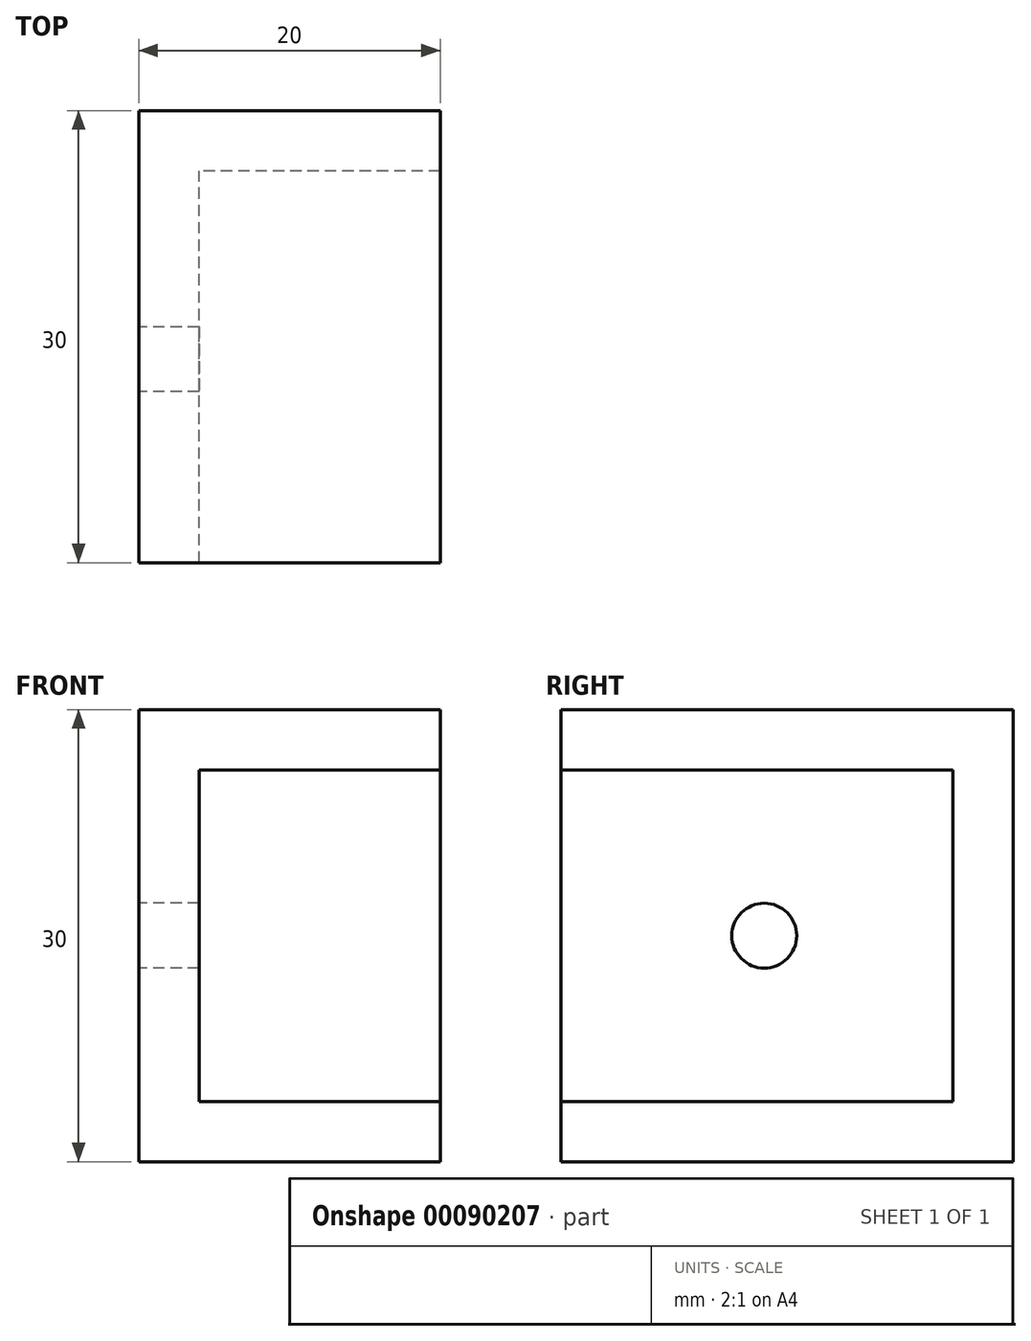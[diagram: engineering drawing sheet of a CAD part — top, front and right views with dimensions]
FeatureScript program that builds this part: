
annotation { "Feature Type Name" : "Feature", "Feature Type Description" : "" }
export const myFeature = defineFeature(function(context is Context, id is Id, definition is map)
    precondition{}
    {
        {
            var Q0;
            Q0=qCreatedBy(makeId("Top.planeOp"),FACE);
            var sketch = newSketch(context, id + "F0", { "sketchPlane" : qUnion([Q0])});
            skLineSegment(sketch, "E0", {"start": v(-8.2, -8.2) * mm, "end": v(-6.57, -8.2) * mm});
            skLineSegment(sketch, "E1", {"start": v(-8.2, -6.57) * mm, "end": v(-8.2, -8.2) * mm});
            skLineSegment(sketch, "E2", {"start": v(-7.66, -6.57) * mm, "end": v(-8.2, -6.57) * mm});
            skLineSegment(sketch, "E3", {"start": v(-6.57, -7.66) * mm, "end": v(-7.66, -6.57) * mm});
            skLineSegment(sketch, "E4", {"start": v(-6.57, -8.2) * mm, "end": v(-6.57, -7.66) * mm});
            skLineSegment(sketch, "E5", {"start": v(7.66, -6.57) * mm, "end": v(6.57, -7.66) * mm});
            skLineSegment(sketch, "E6", {"start": v(8.2, -6.57) * mm, "end": v(7.66, -6.57) * mm});
            skLineSegment(sketch, "E7", {"start": v(8.2, -8.2) * mm, "end": v(8.2, -6.57) * mm});
            skLineSegment(sketch, "E8", {"start": v(6.57, -8.2) * mm, "end": v(8.2, -8.2) * mm});
            skLineSegment(sketch, "E9", {"start": v(6.57, -7.66) * mm, "end": v(6.57, -8.2) * mm});
            skCircle(sketch, "E10", {"center": v(0, 0) * mm, "radius": 2.1 * mm});
            skLineSegment(sketch, "E11", {"start": v(8.2, 8.2) * mm, "end": v(6.57, 8.2) * mm});
            skLineSegment(sketch, "E12", {"start": v(8.2, 6.57) * mm, "end": v(8.2, 8.2) * mm});
            skLineSegment(sketch, "E13", {"start": v(7.66, 6.57) * mm, "end": v(8.2, 6.57) * mm});
            skLineSegment(sketch, "E14", {"start": v(6.57, 7.66) * mm, "end": v(7.66, 6.57) * mm});
            skLineSegment(sketch, "E15", {"start": v(6.57, 8.2) * mm, "end": v(6.57, 7.66) * mm});
            skLineSegment(sketch, "E16", {"start": v(-7.66, 6.57) * mm, "end": v(-6.57, 7.66) * mm});
            skLineSegment(sketch, "E17", {"start": v(-8.2, 6.57) * mm, "end": v(-7.66, 6.57) * mm});
            skLineSegment(sketch, "E18", {"start": v(-8.2, 8.2) * mm, "end": v(-8.2, 6.57) * mm});
            skLineSegment(sketch, "E19", {"start": v(-6.57, 8.2) * mm, "end": v(-8.2, 8.2) * mm});
            skLineSegment(sketch, "E20", {"start": v(-6.57, 7.66) * mm, "end": v(-6.57, 8.2) * mm});
            skLineSegment(sketch, "E21", {"start": v(-6.56, 5.5) * mm, "end": v(-3.4, 2.34) * mm});
            skLineSegment(sketch, "E22", {"start": v(-3.4, 2.34) * mm, "end": v(-3.4, -2.34) * mm});
            skLineSegment(sketch, "E23", {"start": v(-3.4, -2.34) * mm, "end": v(-6.56, -5.5) * mm});
            skLineSegment(sketch, "E24", {"start": v(-6.56, -5.5) * mm, "end": v(-8.2, -5.5) * mm});
            skLineSegment(sketch, "E25", {"start": v(-8.2, -5.5) * mm, "end": v(-8.2, -2.9) * mm});
            skLineSegment(sketch, "E26", {"start": v(-8.2, -2.9) * mm, "end": v(-8.31, -2.9) * mm});
            skLineSegment(sketch, "E27", {"start": v(-8.31, -2.9) * mm, "end": v(-9.77, -4.35) * mm});
            skArc(sketch, "E28", {"start": v(-9.77, -4.35) * mm, "mid": v(-9.94, -4.6) * mm, "end": v(-10, -4.9) * mm});
            skLineSegment(sketch, "E29", {"start": v(-10, -4.9) * mm, "end": v(-10, -8.5) * mm});
            skArc(sketch, "E30", {"start": v(-10, -8.5) * mm, "mid": v(-9.56, -9.56) * mm, "end": v(-8.5, -10) * mm});
            skLineSegment(sketch, "E31", {"start": v(-8.5, -10) * mm, "end": v(-4.9, -10) * mm});
            skArc(sketch, "E32", {"start": v(-4.9, -10) * mm, "mid": v(-4.6, -9.94) * mm, "end": v(-4.35, -9.77) * mm});
            skLineSegment(sketch, "E33", {"start": v(-4.35, -9.77) * mm, "end": v(-2.9, -8.31) * mm});
            skLineSegment(sketch, "E34", {"start": v(-2.9, -8.31) * mm, "end": v(-2.9, -8.2) * mm});
            skLineSegment(sketch, "E35", {"start": v(-2.9, -8.2) * mm, "end": v(-5.5, -8.2) * mm});
            skLineSegment(sketch, "E36", {"start": v(-5.5, -8.2) * mm, "end": v(-5.5, -6.56) * mm});
            skLineSegment(sketch, "E37", {"start": v(-5.5, -6.56) * mm, "end": v(-2.34, -3.4) * mm});
            skLineSegment(sketch, "E38", {"start": v(-2.34, -3.4) * mm, "end": v(2.34, -3.4) * mm});
            skLineSegment(sketch, "E39", {"start": v(2.34, -3.4) * mm, "end": v(5.5, -6.56) * mm});
            skLineSegment(sketch, "E40", {"start": v(5.5, -6.56) * mm, "end": v(5.5, -8.2) * mm});
            skLineSegment(sketch, "E41", {"start": v(5.5, -8.2) * mm, "end": v(2.9, -8.2) * mm});
            skLineSegment(sketch, "E42", {"start": v(2.9, -8.2) * mm, "end": v(2.9, -8.31) * mm});
            skLineSegment(sketch, "E43", {"start": v(2.9, -8.31) * mm, "end": v(4.35, -9.77) * mm});
            skArc(sketch, "E44", {"start": v(4.35, -9.77) * mm, "mid": v(4.6, -9.94) * mm, "end": v(4.9, -10) * mm});
            skLineSegment(sketch, "E45", {"start": v(4.9, -10) * mm, "end": v(8.5, -10) * mm});
            skArc(sketch, "E46", {"start": v(8.5, -10) * mm, "mid": v(9.56, -9.56) * mm, "end": v(10, -8.5) * mm});
            skLineSegment(sketch, "E47", {"start": v(10, -8.5) * mm, "end": v(10, -4.9) * mm});
            skArc(sketch, "E48", {"start": v(10, -4.9) * mm, "mid": v(9.94, -4.6) * mm, "end": v(9.77, -4.35) * mm});
            skLineSegment(sketch, "E49", {"start": v(9.77, -4.35) * mm, "end": v(8.31, -2.9) * mm});
            skLineSegment(sketch, "E50", {"start": v(8.31, -2.9) * mm, "end": v(8.2, -2.9) * mm});
            skLineSegment(sketch, "E51", {"start": v(8.2, -2.9) * mm, "end": v(8.2, -5.5) * mm});
            skLineSegment(sketch, "E52", {"start": v(8.2, -5.5) * mm, "end": v(6.56, -5.5) * mm});
            skLineSegment(sketch, "E53", {"start": v(6.56, -5.5) * mm, "end": v(3.4, -2.34) * mm});
            skLineSegment(sketch, "E54", {"start": v(3.4, -2.34) * mm, "end": v(3.4, 2.34) * mm});
            skLineSegment(sketch, "E55", {"start": v(3.4, 2.34) * mm, "end": v(6.56, 5.5) * mm});
            skLineSegment(sketch, "E56", {"start": v(6.56, 5.5) * mm, "end": v(8.2, 5.5) * mm});
            skLineSegment(sketch, "E57", {"start": v(8.2, 5.5) * mm, "end": v(8.2, 2.9) * mm});
            skLineSegment(sketch, "E58", {"start": v(8.2, 2.9) * mm, "end": v(8.31, 2.9) * mm});
            skLineSegment(sketch, "E59", {"start": v(8.31, 2.9) * mm, "end": v(9.77, 4.35) * mm});
            skArc(sketch, "E60", {"start": v(9.77, 4.35) * mm, "mid": v(9.94, 4.6) * mm, "end": v(10, 4.9) * mm});
            skLineSegment(sketch, "E61", {"start": v(10, 4.9) * mm, "end": v(10, 8.5) * mm});
            skArc(sketch, "E62", {"start": v(10, 8.5) * mm, "mid": v(9.56, 9.56) * mm, "end": v(8.5, 10) * mm});
            skLineSegment(sketch, "E63", {"start": v(8.5, 10) * mm, "end": v(4.9, 10) * mm});
            skArc(sketch, "E64", {"start": v(4.9, 10) * mm, "mid": v(4.6, 9.94) * mm, "end": v(4.35, 9.77) * mm});
            skLineSegment(sketch, "E65", {"start": v(4.35, 9.77) * mm, "end": v(2.9, 8.31) * mm});
            skLineSegment(sketch, "E66", {"start": v(2.9, 8.31) * mm, "end": v(2.9, 8.2) * mm});
            skLineSegment(sketch, "E67", {"start": v(2.9, 8.2) * mm, "end": v(5.5, 8.2) * mm});
            skLineSegment(sketch, "E68", {"start": v(5.5, 8.2) * mm, "end": v(5.5, 6.56) * mm});
            skLineSegment(sketch, "E69", {"start": v(5.5, 6.56) * mm, "end": v(2.34, 3.4) * mm});
            skLineSegment(sketch, "E70", {"start": v(2.34, 3.4) * mm, "end": v(-2.34, 3.4) * mm});
            skLineSegment(sketch, "E71", {"start": v(-2.34, 3.4) * mm, "end": v(-5.5, 6.56) * mm});
            skLineSegment(sketch, "E72", {"start": v(-5.5, 6.56) * mm, "end": v(-5.5, 8.2) * mm});
            skLineSegment(sketch, "E73", {"start": v(-5.5, 8.2) * mm, "end": v(-2.9, 8.2) * mm});
            skLineSegment(sketch, "E74", {"start": v(-2.9, 8.2) * mm, "end": v(-2.9, 8.31) * mm});
            skLineSegment(sketch, "E75", {"start": v(-2.9, 8.31) * mm, "end": v(-4.35, 9.77) * mm});
            skArc(sketch, "E76", {"start": v(-4.35, 9.77) * mm, "mid": v(-4.6, 9.94) * mm, "end": v(-4.9, 10) * mm});
            skLineSegment(sketch, "E77", {"start": v(-4.9, 10) * mm, "end": v(-8.5, 10) * mm});
            skArc(sketch, "E78", {"start": v(-8.5, 10) * mm, "mid": v(-9.56, 9.56) * mm, "end": v(-10, 8.5) * mm});
            skLineSegment(sketch, "E79", {"start": v(-10, 8.5) * mm, "end": v(-10, 4.9) * mm});
            skArc(sketch, "E80", {"start": v(-10, 4.9) * mm, "mid": v(-9.94, 4.6) * mm, "end": v(-9.77, 4.35) * mm});
            skLineSegment(sketch, "E81", {"start": v(-9.77, 4.35) * mm, "end": v(-8.31, 2.9) * mm});
            skLineSegment(sketch, "E82", {"start": v(-8.31, 2.9) * mm, "end": v(-8.2, 2.9) * mm});
            skLineSegment(sketch, "E83", {"start": v(-8.2, 2.9) * mm, "end": v(-8.2, 5.5) * mm});
            skLineSegment(sketch, "E84", {"start": v(-8.2, 5.5) * mm, "end": v(-6.56, 5.5) * mm});
            skSolve(sketch);
        }
        {
            var Q0;
            Q0=qSketchRegion(id+"F0",true);
            extrude(context, id + "F1", {"entities" : qUnion([Q0]), "depth" : 500 * mm});
        }
        {
            var Q0;
            Q0=makeQuery(id+"F1.opExtrude","SWEPT_FACE",FACE,{"disambiguationData":[OSD([sQuery(id+"F0.wireOp",EDGE,"E29")])]});
            var sketch = newSketch(context, id + "F2", { "sketchPlane" : qUnion([Q0])});
            skPoint(sketch, "E85.orphan", {"position": v(-10, 500) * mm});
            skPoint(sketch, "E86.orphan", {"position": v(10, 500) * mm});
            skLineSegment(sketch, "E87.bottom", {"start": v(-10, 18.3) * mm, "end": v(40, 18.3) * mm});
            skLineSegment(sketch, "E87.top", {"start": v(-10, 258.3) * mm, "end": v(40, 258.3) * mm});
            skLineSegment(sketch, "E87.left", {"start": v(-10, 18.3) * mm, "end": v(-10, 258.3) * mm});
            skLineSegment(sketch, "E87.right", {"start": v(40, 18.3) * mm, "end": v(40, 258.3) * mm});
            skCircle(sketch, "E88", {"center": v(26.5, 54.6) * mm, "radius": 2.15 * mm});
            skSolve(sketch);
        }
        {
            var Q0;
            {var subQ0=sQuery(id+"F2.wireOp",EDGE,"E87.right");Q0=makeQuery(id+"F2.imprint","IMPRINT",FACE,{"disambiguationData":[TD([[makeQuery(id+"F2.imprint","IMPRINT",EDGE,{"derivedFrom":subQ0}),1.0]])]});}
            var sketch = newSketch(context, id + "F3", { "sketchPlane" : qUnion([Q0])});
            skCircle(sketch, "E89.0", {"center": v(26.5, 54.6) * mm, "radius": 2.15 * mm});
            skLineSegment(sketch, "E90.0", {"start": v(10, 69.6) * mm, "end": v(10, 39.6) * mm});
            skLineSegment(sketch, "E91.0", {"start": v(40, 39.6) * mm, "end": v(40, 69.6) * mm});
            skLineSegment(sketch, "E92", {"start": v(26.5, 54.6) * mm, "end": v(10, 54.6) * mm, "construction": true});
            skLineSegment(sketch, "E93", {"start": v(40, 39.6) * mm, "end": v(10, 39.6) * mm});
            skLineSegment(sketch, "E94.MirrorCS", {"start": v(40, 69.6) * mm, "end": v(10, 69.6) * mm});
            skPoint(sketch, "E95.orphan", {"position": v(10, 500) * mm});
            skPoint(sketch, "E96.orphan", {"position": v(40, 258.3) * mm});
            skLineSegment(sketch, "E97.0", {"start": v(40, 65.6) * mm, "end": v(14, 65.6) * mm});
            skLineSegment(sketch, "E97.1", {"start": v(14, 65.6) * mm, "end": v(14, 43.6) * mm});
            skLineSegment(sketch, "E97.2", {"start": v(40, 43.6) * mm, "end": v(14, 43.6) * mm});
            skSolve(sketch);
        }
        {
            var Q0;
            Q0=makeQuery(id+"F3.imprint","IMPRINT",FACE,{"disambiguationData":[TD([[makeQuery(id+"F3.imprint","IMPRINT",EDGE,{"derivedFrom":sQuery(id+"F3.wireOp",EDGE,"E90.0")}),1.0]])]});
            var Q1;
            Q1=makeQuery(id+"F3.imprint","IMPRINT",FACE,{"disambiguationData":[TD([[makeQuery(id+"F3.imprint","IMPRINT",EDGE,{"derivedFrom":sQuery(id+"F3.wireOp",EDGE,"E89.0")}),-1.0]])]});
            extrude(context, id + "F4", {"entities" : qUnion([Q0, Q1]), "oppositeDirection" : true, "depth" : 20 * mm});
        }
        {
            var Q0;
            Q0=makeQuery(id+"F4.opExtrude","SWEPT_FACE",FACE,{"disambiguationData":[OSD([sQuery(id+"F3.wireOp",EDGE,"E93")])]});
            var sketch = newSketch(context, id + "F5", { "sketchPlane" : qUnion([Q0])});
            skLineSegment(sketch, "E98.0", {"start": v(-10, 40) * mm, "end": v(-10, 10) * mm});
            skLineSegment(sketch, "E99.0", {"start": v(10, 10) * mm, "end": v(-10, 10) * mm});
            skLineSegment(sketch, "E100", {"start": v(-10, 40) * mm, "end": v(-6, 40) * mm});
            skLineSegment(sketch, "E101", {"start": v(10, 14) * mm, "end": v(10, 10) * mm});
            skLineSegment(sketch, "E102", {"start": v(-10, 40) * mm, "end": v(10, 10) * mm, "construction": true});
            skSolve(sketch);
        }
        {
            var Q0;
            Q0=makeQuery(id+"F5.imprint","IMPRINT",FACE,{"disambiguationData":[TD([[makeQuery(id+"F5.imprint","IMPRINT",EDGE,{"derivedFrom":sQuery(id+"F5.wireOp",EDGE,"E98.0")}),1.0]])]});
            var Q1;
            Q1=makeQuery(id+"F4.opExtrude","SWEPT_BODY",BODY,{"disambiguationData":[OSD([sQuery(id+"F3.wireOp",EDGE,"E89.0"),sQuery(id+"F3.wireOp",EDGE,"E90.0"),sQuery(id+"F3.wireOp",EDGE,"E91.0"),sQuery(id+"F3.wireOp",EDGE,"E93"),sQuery(id+"F3.wireOp",EDGE,"E94.MirrorCS")])]});
            extrude(context, id + "F6", {"entities" : qUnion([Q0]), "operationType" : NewBodyOperationType.INTERSECT, "endBound" : BoundingType.UP_TO_BODY, "oppositeDirection" : true, "endBoundEntityBody" : qUnion([Q1]), "depth" : 25 * mm});
        }
        {
            var Q0;
            Q0=makeQuery(id+"F3.imprint","IMPRINT",FACE,{"disambiguationData":[TD([[makeQuery(id+"F3.imprint","IMPRINT",EDGE,{"derivedFrom":sQuery(id+"F3.wireOp",EDGE,"E89.0")}),-1.0]])]});
            var Q1;
            Q1=makeQuery(id+"F4.opExtrude","CAP_FACE",FACE,{"disambiguationData":[OSD([sQuery(id+"F3.wireOp",EDGE,"E89.0"),sQuery(id+"F3.wireOp",EDGE,"E90.0"),sQuery(id+"F3.wireOp",EDGE,"E91.0"),sQuery(id+"F3.wireOp",EDGE,"E93"),sQuery(id+"F3.wireOp",EDGE,"E94.MirrorCS")])],"isStart":false});
            var Q2;
            Q2=makeQuery(id+"F4.opExtrude","CAP_FACE",FACE,{"disambiguationData":[OSD([sQuery(id+"F3.wireOp",EDGE,"E89.0"),sQuery(id+"F3.wireOp",EDGE,"E90.0"),sQuery(id+"F3.wireOp",EDGE,"E91.0"),sQuery(id+"F3.wireOp",EDGE,"E93"),sQuery(id+"F3.wireOp",EDGE,"E94.MirrorCS")])],"isStart":false});
            extrude(context, id + "F7", {"entities" : qUnion([Q0]), "operationType" : NewBodyOperationType.REMOVE, "endBound" : BoundingType.UP_TO_SURFACE, "oppositeDirection" : true, "endBoundEntityFace" : qUnion([Q1]), "depth" : 4 * mm, "hasSecondDirection" : true, "secondDirectionOppositeDirection" : true, "secondDirectionBoundEntityFace" : qUnion([Q2]), "secondDirectionDepth" : 4 * mm});
        }
    });
